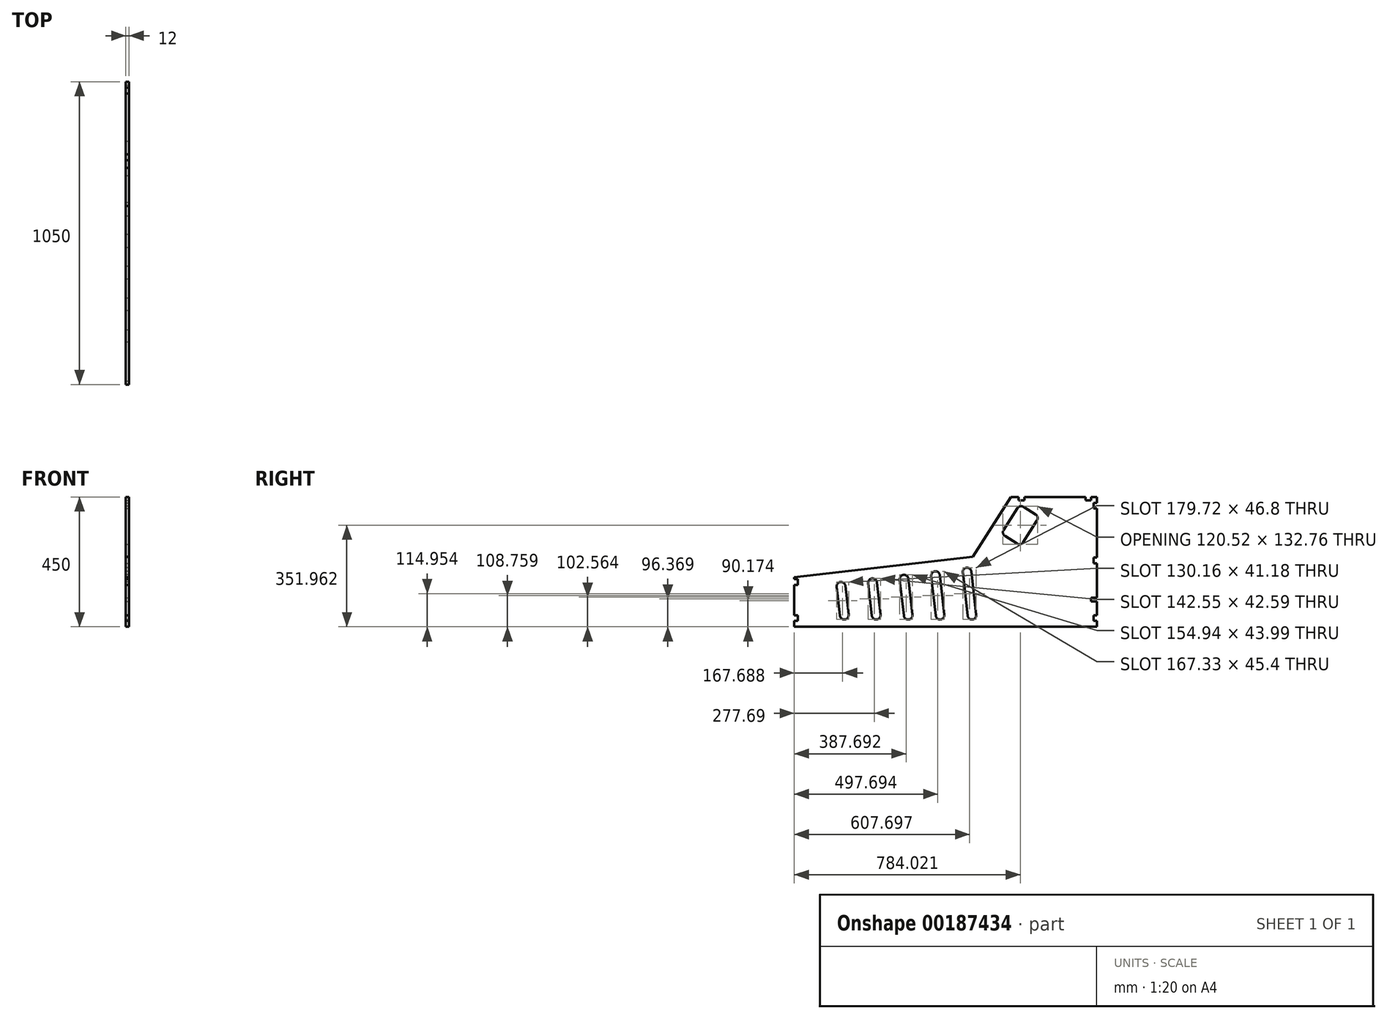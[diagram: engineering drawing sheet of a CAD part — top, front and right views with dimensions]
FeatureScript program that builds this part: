
annotation { "Feature Type Name" : "Feature", "Feature Type Description" : "" }
export const myFeature = defineFeature(function(context is Context, id is Id, definition is map)
    precondition{}
    {
        {
            var Q0;
            Q0=qCreatedBy(makeId("Right.planeOp"),FACE);
            var sketch = newSketch(context, id + "F0", { "sketchPlane" : qUnion([Q0])});
            skLineSegment(sketch, "E0.bottom", {"start": v(0, 0) * mm, "end": v(-738, 0) * mm});
            skLineSegment(sketch, "E0.top", {"start": v(0, 460) * mm, "end": v(-738, 460) * mm});
            skLineSegment(sketch, "E0.left", {"start": v(0, 0) * mm, "end": v(0, 460) * mm});
            skLineSegment(sketch, "E0.right", {"start": v(-738, 0) * mm, "end": v(-738, 460) * mm});
            skLineSegment(sketch, "E1", {"start": v(-100.56, 446.57) * mm, "end": v(-230.57, 242.52) * mm});
            skLineSegment(sketch, "E2", {"start": v(-230.57, 242.52) * mm, "end": v(-738, 185) * mm});
            skLineSegment(sketch, "E3", {"start": v(-100.56, 446.57) * mm, "end": v(-92, 460) * mm});
            skLineSegment(sketch, "E4.bottom", {"start": v(0, 0) * mm, "end": v(200, 0) * mm});
            skLineSegment(sketch, "E4.top", {"start": v(0, 460) * mm, "end": v(200, 460) * mm});
            skLineSegment(sketch, "E4.right", {"start": v(200, 0) * mm, "end": v(200, 460) * mm});
            skLineSegment(sketch, "E5", {"start": v(-738, 134.68) * mm, "end": v(-63.78, 211.1) * mm});
            skLineSegment(sketch, "E6", {"start": v(-32.71, 460) * mm, "end": v(-265.98, 93.9) * mm});
            skLineSegment(sketch, "E7", {"start": v(-67.47, 424.06) * mm, "end": v(0, 381.07) * mm});
            skLineSegment(sketch, "E8", {"start": v(0, 381.07) * mm, "end": v(-64.49, 279.87) * mm});
            skLineSegment(sketch, "E9", {"start": v(-67.47, 424.06) * mm, "end": v(-131.95, 322.86) * mm});
            skLineSegment(sketch, "E10", {"start": v(-64.49, 279.87) * mm, "end": v(-131.95, 322.86) * mm});
            skLineSegment(sketch, "E11", {"start": v(-688, 140.35) * mm, "end": v(-676.62, 40) * mm});
            skLineSegment(sketch, "E12", {"start": v(-578.7, 152.74) * mm, "end": v(-565.92, 40) * mm});
            skLineSegment(sketch, "E13", {"start": v(-469.4, 165.13) * mm, "end": v(-455.22, 40) * mm});
            skLineSegment(sketch, "E14", {"start": v(-360.1, 177.52) * mm, "end": v(-344.51, 40) * mm});
            skLineSegment(sketch, "E15", {"start": v(-250.8, 189.9) * mm, "end": v(-233.8, 40) * mm});
            skCircle(sketch, "E16", {"center": v(-688, 140.35) * mm, "radius": 15 * mm});
            skCircle(sketch, "E17", {"center": v(-676.62, 40) * mm, "radius": 15 * mm});
            skCircle(sketch, "E18", {"center": v(-565.92, 40) * mm, "radius": 15 * mm});
            skCircle(sketch, "E19", {"center": v(-578.7, 152.74) * mm, "radius": 15 * mm});
            skCircle(sketch, "E20", {"center": v(-469.4, 165.13) * mm, "radius": 15 * mm});
            skCircle(sketch, "E21", {"center": v(-360.1, 177.52) * mm, "radius": 15 * mm});
            skCircle(sketch, "E22", {"center": v(-455.22, 40) * mm, "radius": 15 * mm});
            skCircle(sketch, "E23", {"center": v(-344.51, 40) * mm, "radius": 15 * mm});
            skCircle(sketch, "E24", {"center": v(-233.8, 40) * mm, "radius": 15 * mm});
            skCircle(sketch, "E25", {"center": v(-250.8, 189.9) * mm, "radius": 15 * mm});
            skLineSegment(sketch, "E26", {"start": v(-688, 140.35) * mm, "end": v(-250.8, 189.9) * mm});
            skLineSegment(sketch, "E27", {"start": v(-233.8, 40) * mm, "end": v(-676.62, 40) * mm});
            skLineSegment(sketch, "E28", {"start": v(-673.1, 142.04) * mm, "end": v(-661.72, 41.69) * mm});
            skLineSegment(sketch, "E29", {"start": v(-688, 140.35) * mm, "end": v(-702.9, 138.66) * mm});
            skLineSegment(sketch, "E30", {"start": v(-702.9, 138.66) * mm, "end": v(-691.53, 38.31) * mm});
            skLineSegment(sketch, "E31", {"start": v(-563.8, 154.43) * mm, "end": v(-551.02, 41.69) * mm});
            skLineSegment(sketch, "E32", {"start": v(-484.3, 163.44) * mm, "end": v(-470.12, 38.31) * mm});
            skLineSegment(sketch, "E33", {"start": v(-593.6, 151.05) * mm, "end": v(-580.82, 38.31) * mm});
            skLineSegment(sketch, "E34", {"start": v(-375, 175.83) * mm, "end": v(-359.42, 38.31) * mm});
            skLineSegment(sketch, "E35", {"start": v(-345.2, 179.2) * mm, "end": v(-329.6, 41.69) * mm});
            skLineSegment(sketch, "E36", {"start": v(-265.7, 188.22) * mm, "end": v(-248.71, 38.31) * mm});
            skLineSegment(sketch, "E37", {"start": v(-250.8, 189.9) * mm, "end": v(-235.9, 191.6) * mm});
            skLineSegment(sketch, "E38", {"start": v(-235.9, 191.6) * mm, "end": v(-218.9, 41.69) * mm});
            skLineSegment(sketch, "E39", {"start": v(-454.5, 166.82) * mm, "end": v(-440.31, 41.69) * mm});
            skLineSegment(sketch, "E40", {"start": v(-738, 185) * mm, "end": v(-850, 172.3) * mm});
            skLineSegment(sketch, "E41", {"start": v(-850, 172.3) * mm, "end": v(-850, 0) * mm});
            skLineSegment(sketch, "E42", {"start": v(-850, 0) * mm, "end": v(-738, 0) * mm});
            skSolve(sketch);
        }
        {
            var Q0;
            Q0=makeQuery(id+"F0.imprint","IMPRINT",FACE,{"disambiguationData":[TD([[makeQuery(id+"F0.imprint","IMPRINT",EDGE,{"derivedFrom":sQuery(id+"F0.wireOp",EDGE,"E1")}),1.0]])]});
            var Q1;
            {var subQ0=sQuery(id+"F0.wireOp",EDGE,"E28");var subQ1=sQuery(id+"F0.wireOp",EDGE,"E5");var subQ2=makeQuery(id+"F0.imprint","INTERSECT",VERTEX,{"derivedFrom":[subQ1,subQ0]});Q1=makeQuery(id+"F0.imprint","IMPRINT",FACE,{"disambiguationData":[TD([[makeQuery(id+"F0.imprint","IMPRINT",EDGE,{"disambiguationData":[TD([[subQ2,-1.0]])],"derivedFrom":subQ1}),1.0]])]});}
            var Q2;
            {var subQ0=sQuery(id+"F0.wireOp",EDGE,"E28");var subQ3=sQuery(id+"F0.wireOp",EDGE,"E5");var subQ4=makeQuery(id+"F0.imprint","INTERSECT",VERTEX,{"derivedFrom":[subQ3,subQ0]});Q2=makeQuery(id+"F0.imprint","IMPRINT",FACE,{"disambiguationData":[TD([[makeQuery(id+"F0.imprint","IMPRINT",EDGE,{"disambiguationData":[TD([[subQ4,-1.0]])],"derivedFrom":subQ3}),-1.0]])]});}
            var Q3;
            {var subQ34=sQuery(id+"F0.wireOp",EDGE,"E0.bottom");Q3=makeQuery(id+"F0.imprint","IMPRINT",FACE,{"disambiguationData":[TD([[makeQuery(id+"F0.imprint","IMPRINT",EDGE,{"derivedFrom":subQ34}),-1.0]])]});}
            var Q4;
            {var subQ5=sQuery(id+"F0.wireOp",EDGE,"E31");var subQ7=sQuery(id+"F0.wireOp",EDGE,"E5");var subQ8=makeQuery(id+"F0.imprint","INTERSECT",VERTEX,{"derivedFrom":[subQ7,subQ5]});Q4=makeQuery(id+"F0.imprint","IMPRINT",FACE,{"disambiguationData":[TD([[makeQuery(id+"F0.imprint","IMPRINT",EDGE,{"disambiguationData":[TD([[subQ8,-1.0]])],"derivedFrom":subQ7}),-1.0]])]});}
            var Q5;
            {var subQ0=sQuery(id+"F0.wireOp",EDGE,"E31");var subQ1=sQuery(id+"F0.wireOp",EDGE,"E5");var subQ2=makeQuery(id+"F0.imprint","INTERSECT",VERTEX,{"derivedFrom":[subQ1,subQ0]});Q5=makeQuery(id+"F0.imprint","IMPRINT",FACE,{"disambiguationData":[TD([[makeQuery(id+"F0.imprint","IMPRINT",EDGE,{"disambiguationData":[TD([[subQ2,-1.0]])],"derivedFrom":subQ1}),1.0]])]});}
            var Q6;
            {var subQ0=sQuery(id+"F0.wireOp",EDGE,"E39");var subQ1=sQuery(id+"F0.wireOp",EDGE,"E5");var subQ2=makeQuery(id+"F0.imprint","INTERSECT",VERTEX,{"derivedFrom":[subQ1,subQ0]});Q6=makeQuery(id+"F0.imprint","IMPRINT",FACE,{"disambiguationData":[TD([[makeQuery(id+"F0.imprint","IMPRINT",EDGE,{"disambiguationData":[TD([[subQ2,-1.0]])],"derivedFrom":subQ1}),1.0]])]});}
            var Q7;
            {var subQ1=sQuery(id+"F0.wireOp",EDGE,"E5");var subQ7=sQuery(id+"F0.wireOp",EDGE,"E39");var subQ9=makeQuery(id+"F0.imprint","INTERSECT",VERTEX,{"derivedFrom":[subQ1,subQ7]});Q7=makeQuery(id+"F0.imprint","IMPRINT",FACE,{"disambiguationData":[TD([[makeQuery(id+"F0.imprint","IMPRINT",EDGE,{"disambiguationData":[TD([[subQ9,-1.0]])],"derivedFrom":subQ1}),-1.0]])]});}
            var Q8;
            {var subQ0=sQuery(id+"F0.wireOp",EDGE,"E35");var subQ3=sQuery(id+"F0.wireOp",EDGE,"E5");var subQ4=makeQuery(id+"F0.imprint","INTERSECT",VERTEX,{"derivedFrom":[subQ3,subQ0]});Q8=makeQuery(id+"F0.imprint","IMPRINT",FACE,{"disambiguationData":[TD([[makeQuery(id+"F0.imprint","IMPRINT",EDGE,{"disambiguationData":[TD([[subQ4,-1.0]])],"derivedFrom":subQ3}),-1.0]])]});}
            var Q9;
            {var subQ0=sQuery(id+"F0.wireOp",EDGE,"E35");var subQ1=sQuery(id+"F0.wireOp",EDGE,"E5");var subQ2=makeQuery(id+"F0.imprint","INTERSECT",VERTEX,{"derivedFrom":[subQ1,subQ0]});Q9=makeQuery(id+"F0.imprint","IMPRINT",FACE,{"disambiguationData":[TD([[makeQuery(id+"F0.imprint","IMPRINT",EDGE,{"disambiguationData":[TD([[subQ2,-1.0]])],"derivedFrom":subQ1}),1.0]])]});}
            var Q10;
            {var subQ0=sQuery(id+"F0.wireOp",EDGE,"E6");var subQ1=sQuery(id+"F0.wireOp",EDGE,"E5");var subQ2=makeQuery(id+"F0.imprint","INTERSECT",VERTEX,{"derivedFrom":[subQ1,subQ0]});Q10=makeQuery(id+"F0.imprint","IMPRINT",FACE,{"disambiguationData":[TD([[makeQuery(id+"F0.imprint","IMPRINT",EDGE,{"disambiguationData":[TD([[subQ2,1.0]])],"derivedFrom":subQ1}),-1.0]])]});}
            var Q11;
            {var subQ4=sQuery(id+"F0.wireOp",EDGE,"E4.bottom");Q11=makeQuery(id+"F0.imprint","IMPRINT",FACE,{"disambiguationData":[TD([[makeQuery(id+"F0.imprint","IMPRINT",EDGE,{"derivedFrom":subQ4}),1.0]])]});}
            var Q12;
            {var subQ0=sQuery(id+"F0.wireOp",EDGE,"E28");Q12=makeQuery(id+"F0.imprint","IMPRINT",FACE,{"disambiguationData":[TD([[makeQuery(id+"F0.imprint","IMPRINT",EDGE,{"derivedFrom":subQ0}),1.0]])]});}
            var Q13;
            {var subQ0=sQuery(id+"F0.wireOp",EDGE,"E31");Q13=makeQuery(id+"F0.imprint","IMPRINT",FACE,{"disambiguationData":[TD([[makeQuery(id+"F0.imprint","IMPRINT",EDGE,{"derivedFrom":subQ0}),1.0]])]});}
            var Q14;
            {var subQ5=sQuery(id+"F0.wireOp",EDGE,"E39");Q14=makeQuery(id+"F0.imprint","IMPRINT",FACE,{"disambiguationData":[TD([[makeQuery(id+"F0.imprint","IMPRINT",EDGE,{"derivedFrom":subQ5}),1.0]])]});}
            var Q15;
            {var subQ5=sQuery(id+"F0.wireOp",EDGE,"E35");Q15=makeQuery(id+"F0.imprint","IMPRINT",FACE,{"disambiguationData":[TD([[makeQuery(id+"F0.imprint","IMPRINT",EDGE,{"derivedFrom":subQ5}),1.0]])]});}
            var Q16;
            {var subQ1=sQuery(id+"F0.wireOp",EDGE,"E0.top");var subQ3=sQuery(id+"F0.wireOp",EDGE,"E6");var subQ4=makeQuery(id+"F0.imprint","INTERSECT",VERTEX,{"derivedFrom":[subQ1,subQ3]});Q16=makeQuery(id+"F0.imprint","IMPRINT",FACE,{"disambiguationData":[TD([[makeQuery(id+"F0.imprint","IMPRINT",EDGE,{"disambiguationData":[TD([[subQ4,1.0]])],"derivedFrom":subQ1}),1.0]])]});}
            var Q17;
            {var subQ0=sQuery(id+"F0.wireOp",EDGE,"E40");Q17=makeQuery(id+"F0.imprint","IMPRINT",FACE,{"disambiguationData":[TD([[makeQuery(id+"F0.imprint","IMPRINT",EDGE,{"derivedFrom":subQ0}),1.0]])]});}
            extrude(context, id + "F1", {"entities" : qUnion([Q0, Q1, Q2, Q3, Q4, Q5, Q6, Q7, Q8, Q9, Q10, Q11, Q12, Q13, Q14, Q15, Q16, Q17]), "depth" : 12 * mm, "offsetDistance" : 25 * mm});
        }
        {
            var Q0;
            Q0=makeQuery(id+"F1.opExtrude","CAP_FACE",FACE,{"disambiguationData":[OSD([sQuery(id+"F0.wireOp",EDGE,"E0.bottom"),sQuery(id+"F0.wireOp",EDGE,"E0.top"),sQuery(id+"F0.wireOp",EDGE,"E0.right"),sQuery(id+"F0.wireOp",EDGE,"E1"),sQuery(id+"F0.wireOp",EDGE,"E2"),sQuery(id+"F0.wireOp",EDGE,"E3"),sQuery(id+"F0.wireOp",EDGE,"E4.bottom"),sQuery(id+"F0.wireOp",EDGE,"E4.top"),sQuery(id+"F0.wireOp",EDGE,"E4.right")])],"isStart":false});
            var sketch = newSketch(context, id + "F2", { "sketchPlane" : qUnion([Q0])});
            skLineSegment(sketch, "E43.bottom", {"start": v(-850, 20) * mm, "end": v(-838, 20) * mm});
            skLineSegment(sketch, "E43.top", {"start": v(-850, 40) * mm, "end": v(-838, 40) * mm});
            skLineSegment(sketch, "E43.left", {"start": v(-850, 20) * mm, "end": v(-850, 40) * mm});
            skLineSegment(sketch, "E43.right", {"start": v(-838, 20) * mm, "end": v(-838, 40) * mm});
            skLineSegment(sketch, "E44.bottom", {"start": v(-850, 145) * mm, "end": v(-838, 145) * mm});
            skLineSegment(sketch, "E44.top", {"start": v(-850, 165) * mm, "end": v(-838, 165) * mm});
            skLineSegment(sketch, "E44.left", {"start": v(-850, 145) * mm, "end": v(-850, 165) * mm});
            skLineSegment(sketch, "E44.right", {"start": v(-838, 145) * mm, "end": v(-838, 165) * mm});
            skLineSegment(sketch, "E45.bottom", {"start": v(200, 20) * mm, "end": v(188, 20) * mm});
            skLineSegment(sketch, "E45.top", {"start": v(200, 40) * mm, "end": v(188, 40) * mm});
            skLineSegment(sketch, "E45.left", {"start": v(200, 20) * mm, "end": v(200, 40) * mm});
            skLineSegment(sketch, "E45.right", {"start": v(188, 20) * mm, "end": v(188, 40) * mm});
            skLineSegment(sketch, "E46.bottom", {"start": v(200, 220) * mm, "end": v(188, 220) * mm});
            skLineSegment(sketch, "E46.top", {"start": v(200, 240) * mm, "end": v(188, 240) * mm});
            skLineSegment(sketch, "E46.left", {"start": v(200, 220) * mm, "end": v(200, 240) * mm});
            skLineSegment(sketch, "E46.right", {"start": v(188, 220) * mm, "end": v(188, 240) * mm});
            skLineSegment(sketch, "E47.bottom", {"start": v(200, 410) * mm, "end": v(188, 410) * mm});
            skLineSegment(sketch, "E47.top", {"start": v(200, 430) * mm, "end": v(188, 430) * mm});
            skLineSegment(sketch, "E47.left", {"start": v(200, 410) * mm, "end": v(200, 430) * mm});
            skLineSegment(sketch, "E47.right", {"start": v(188, 410) * mm, "end": v(188, 430) * mm});
            skLineSegment(sketch, "E48.bottom", {"start": v(180, 460) * mm, "end": v(160, 460) * mm});
            skLineSegment(sketch, "E48.top", {"start": v(180, 438) * mm, "end": v(160, 438) * mm});
            skLineSegment(sketch, "E48.left", {"start": v(180, 460) * mm, "end": v(180, 438) * mm});
            skLineSegment(sketch, "E48.right", {"start": v(160, 460) * mm, "end": v(160, 438) * mm});
            skLineSegment(sketch, "E49.bottom", {"start": v(-72, 460) * mm, "end": v(-52, 460) * mm});
            skLineSegment(sketch, "E49.top", {"start": v(-72, 438) * mm, "end": v(-52, 438) * mm});
            skLineSegment(sketch, "E49.left", {"start": v(-72, 460) * mm, "end": v(-72, 438) * mm});
            skLineSegment(sketch, "E49.right", {"start": v(-52, 460) * mm, "end": v(-52, 438) * mm});
            skSolve(sketch);
        }
        {
            var Q0;
            Q0=qSketchRegion(id+"F2",true);
            extrude(context, id + "F3", {"entities" : qUnion([Q0]), "operationType" : NewBodyOperationType.REMOVE, "oppositeDirection" : true, "depth" : 25 * mm});
        }
        {
            var Q0;
            Q0=makeQuery(id+"F1.opExtrude","SWEPT_EDGE",EDGE,{"disambiguationData":[OSD([sQuery(id+"F0.wireOp",EDGE,"E7"),sQuery(id+"F0.wireOp",EDGE,"E9")])]});
            var Q1;
            Q1=makeQuery(id+"F1.opExtrude","SWEPT_EDGE",EDGE,{"disambiguationData":[OSD([sQuery(id+"F0.wireOp",EDGE,"E9"),sQuery(id+"F0.wireOp",EDGE,"E10")])]});
            var Q2;
            Q2=makeQuery(id+"F1.opExtrude","SWEPT_EDGE",EDGE,{"disambiguationData":[OSD([sQuery(id+"F0.wireOp",EDGE,"E7"),sQuery(id+"F0.wireOp",EDGE,"E8")])]});
            var Q3;
            Q3=makeQuery(id+"F1.opExtrude","SWEPT_EDGE",EDGE,{"disambiguationData":[OSD([sQuery(id+"F0.wireOp",EDGE,"E8"),sQuery(id+"F0.wireOp",EDGE,"E10")])]});
            fillet(context, id + "F4", {"entities" : qUnion([Q0, Q1, Q2, Q3]), "radius" : 15 * mm, "tangentPropagation" : true, "allowEdgeOverflow" : false});
        }
        {
            var Q0;
            Q0=makeQuery(id+"F1.opExtrude","CAP_FACE",FACE,{"disambiguationData":[OSD([sQuery(id+"F0.wireOp",EDGE,"E0.bottom"),sQuery(id+"F0.wireOp",EDGE,"E0.top"),sQuery(id+"F0.wireOp",EDGE,"E0.right"),sQuery(id+"F0.wireOp",EDGE,"E1"),sQuery(id+"F0.wireOp",EDGE,"E2"),sQuery(id+"F0.wireOp",EDGE,"E3"),sQuery(id+"F0.wireOp",EDGE,"E4.bottom"),sQuery(id+"F0.wireOp",EDGE,"E4.top"),sQuery(id+"F0.wireOp",EDGE,"E4.right"),sQuery(id+"F0.wireOp",EDGE,"E7"),sQuery(id+"F0.wireOp",EDGE,"E8"),sQuery(id+"F0.wireOp",EDGE,"E9"),sQuery(id+"F0.wireOp",EDGE,"E10"),sQuery(id+"F0.wireOp",EDGE,"E16"),sQuery(id+"F0.wireOp",EDGE,"E17"),sQuery(id+"F0.wireOp",EDGE,"E18"),sQuery(id+"F0.wireOp",EDGE,"E19"),sQuery(id+"F0.wireOp",EDGE,"E20"),sQuery(id+"F0.wireOp",EDGE,"E21"),sQuery(id+"F0.wireOp",EDGE,"E22"),sQuery(id+"F0.wireOp",EDGE,"E23"),sQuery(id+"F0.wireOp",EDGE,"E24"),sQuery(id+"F0.wireOp",EDGE,"E25"),sQuery(id+"F0.wireOp",EDGE,"E28"),sQuery(id+"F0.wireOp",EDGE,"E30"),sQuery(id+"F0.wireOp",EDGE,"E31"),sQuery(id+"F0.wireOp",EDGE,"E32"),sQuery(id+"F0.wireOp",EDGE,"E33"),sQuery(id+"F0.wireOp",EDGE,"E34"),sQuery(id+"F0.wireOp",EDGE,"E35"),sQuery(id+"F0.wireOp",EDGE,"E36"),sQuery(id+"F0.wireOp",EDGE,"E38"),sQuery(id+"F0.wireOp",EDGE,"E39")])],"isStart":false});
            var sketch = newSketch(context, id + "F5", { "sketchPlane" : qUnion([Q0])});
            skLineSegment(sketch, "E50.bottom", {"start": v(200, 88) * mm, "end": v(180, 88) * mm});
            skLineSegment(sketch, "E50.top", {"start": v(200, 100) * mm, "end": v(180, 100) * mm});
            skLineSegment(sketch, "E50.left", {"start": v(200, 88) * mm, "end": v(200, 100) * mm});
            skLineSegment(sketch, "E50.right", {"start": v(180, 88) * mm, "end": v(180, 100) * mm});
            skSolve(sketch);
        }
        {
            var Q0;
            Q0=makeQuery(id+"F5.imprint","IMPRINT",FACE,{"disambiguationData":[TD([[makeQuery(id+"F5.imprint","IMPRINT",EDGE,{"derivedFrom":sQuery(id+"F5.wireOp",EDGE,"E50.bottom")}),-1.0]])]});
            extrude(context, id + "F6", {"entities" : qUnion([Q0]), "operationType" : NewBodyOperationType.REMOVE, "oppositeDirection" : true, "depth" : 25 * mm, "offsetDistance" : 25 * mm});
        }
        {
            var Q0;
            {var subQ25=sQuery(id+"F0.wireOp",EDGE,"E4.top");var subQ31=sQuery(id+"F0.wireOp",EDGE,"E0.top");Q0=makeQuery(id+"F3.boolean.opBoolean","SPLIT",FACE,{"disambiguationData":[TD([makeQuery(id+"F3.opExtrude","SWEPT_FACE",FACE,{"disambiguationData":[OSD([sQuery(id+"F2.wireOp",EDGE,"E49.left")])]})])],"derivedFrom":makeQuery(id+"F1.opExtrude","SWEPT_FACE",FACE,{"disambiguationData":[OSD([subQ31,subQ25])]})});}
            var Q1;
            {var subQ25=sQuery(id+"F0.wireOp",EDGE,"E4.top");var subQ31=sQuery(id+"F0.wireOp",EDGE,"E0.top");Q1=makeQuery(id+"F3.boolean.opBoolean","SPLIT",FACE,{"disambiguationData":[TD([makeQuery(id+"F3.opExtrude","SWEPT_FACE",FACE,{"disambiguationData":[OSD([sQuery(id+"F2.wireOp",EDGE,"E48.right")])]})])],"derivedFrom":makeQuery(id+"F1.opExtrude","SWEPT_FACE",FACE,{"disambiguationData":[OSD([subQ31,subQ25])]})});}
            var Q2;
            {var subQ24=sQuery(id+"F0.wireOp",EDGE,"E4.right");var subQ25=sQuery(id+"F0.wireOp",EDGE,"E4.top");var subQ31=sQuery(id+"F0.wireOp",EDGE,"E0.top");Q2=makeQuery(id+"F3.boolean.opBoolean","SPLIT",FACE,{"disambiguationData":[TD([makeQuery(id+"F1.opExtrude","SWEPT_FACE",FACE,{"disambiguationData":[OSD([subQ24])]})])],"derivedFrom":makeQuery(id+"F1.opExtrude","SWEPT_FACE",FACE,{"disambiguationData":[OSD([subQ31,subQ25])]})});}
            extrude(context, id + "F7", {"entities" : qUnion([Q0, Q1, Q2]), "operationType" : NewBodyOperationType.REMOVE, "oppositeDirection" : true, "depth" : 10 * mm, "offsetDistance" : 25 * mm});
        }
        {
            var Q0;
            Q0=makeQuery(id+"F7.boolean.opBoolean","COPY",FACE,{"derivedFrom":makeQuery(id+"F7.opExtrude","SWEPT_FACE",FACE,{"disambiguationData":[OSD([sQuery(id+"F0.wireOp",EDGE,"E0.top"),sQuery(id+"F0.wireOp",EDGE,"E3")])]})});
            extrude(context, id + "F8", {"entities" : qUnion([Q0]), "operationType" : NewBodyOperationType.REMOVE, "oppositeDirection" : true, "depth" : 25 * mm, "offsetDistance" : 25 * mm});
        }
    });
